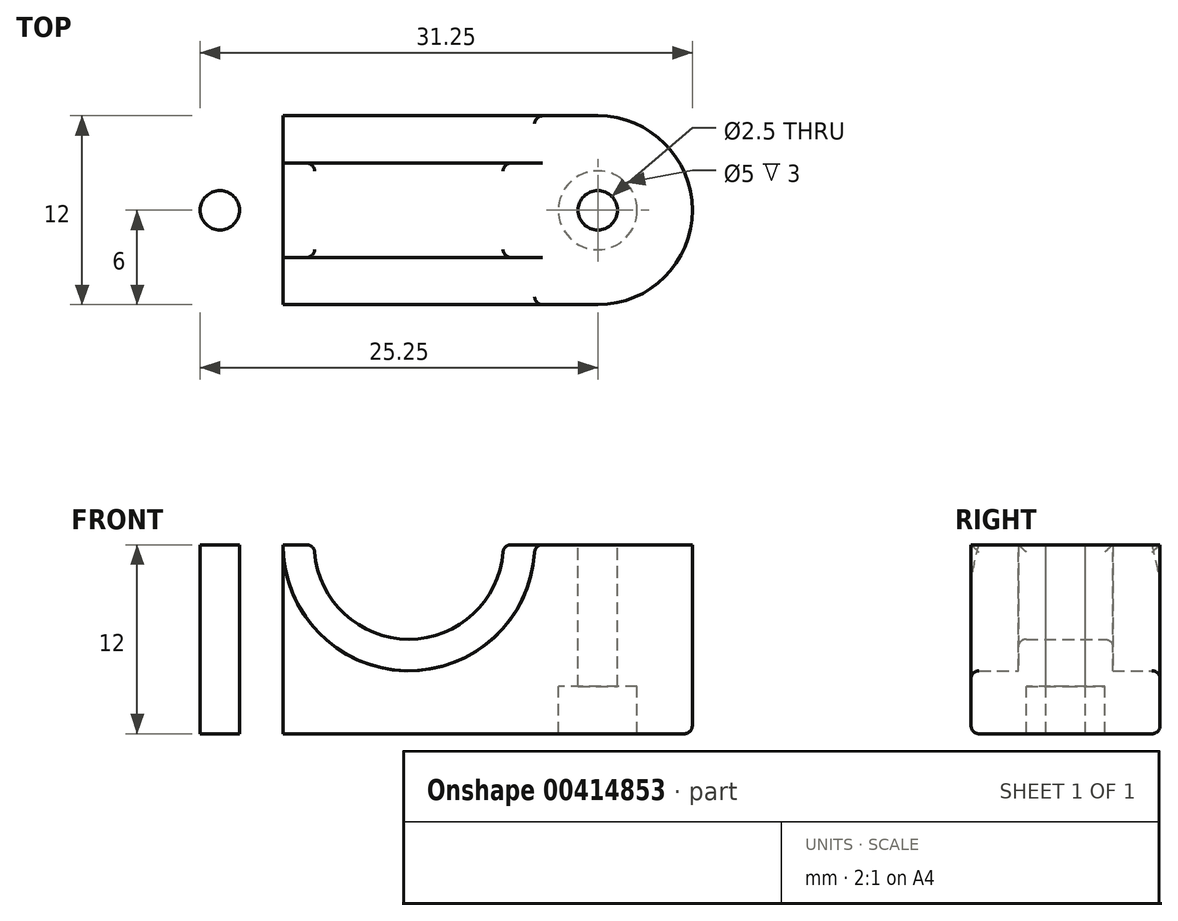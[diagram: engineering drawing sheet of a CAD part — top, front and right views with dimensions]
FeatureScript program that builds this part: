
annotation { "Feature Type Name" : "Feature", "Feature Type Description" : "" }
export const myFeature = defineFeature(function(context is Context, id is Id, definition is map)
    precondition{}
    {
        {
            var Q0;
            Q0=qCreatedBy(makeId("Top.planeOp"),FACE);
            cPlane(context, id + "F0", {"entities" : qUnion([Q0]), "cplaneType" : CPlaneType.OFFSET, "offset" : 1.5 * mm, "oppositeDirection" : true, "width" : 150 * mm, "height" : 150 * mm});
        }
        {
            var Q0;
            Q0=qCreatedBy(makeId("Front.planeOp"),FACE);
            cPlane(context, id + "F1", {"entities" : qUnion([Q0]), "cplaneType" : CPlaneType.OFFSET, "offset" : 12 * mm, "width" : 150 * mm, "height" : 150 * mm});
        }
        {
            var Q0;
            Q0=qCreatedBy(id+"F0.planeOp",FACE);
            var sketch = newSketch(context, id + "F2", { "sketchPlane" : qUnion([Q0])});
            skLineSegment(sketch, "E0.bottom", {"start": v(18, 18) * mm, "end": v(-18, 18) * mm, "construction": true});
            skLineSegment(sketch, "E0.left", {"start": v(18, 18) * mm, "end": v(18, -18) * mm, "construction": true});
            skLineSegment(sketch, "E0.right", {"start": v(-18, 18) * mm, "end": v(-18, -18) * mm, "construction": true});
            skPoint(sketch, "E0.middle", {"position": v(0, 0) * mm});
            skLineSegment(sketch, "E1", {"start": v(-18, 0) * mm, "end": v(18, 0) * mm, "construction": true});
            skLineSegment(sketch, "E2", {"start": v(0, 18) * mm, "end": v(0, -18) * mm, "construction": true});
            skCircle(sketch, "E3", {"center": v(12, -12) * mm, "radius": 1.25 * mm});
            skCircle(sketch, "E4.MirrorC", {"center": v(-12, -12) * mm, "radius": 1.25 * mm});
            skCircle(sketch, "E5", {"center": v(12, 0) * mm, "radius": 1.25 * mm});
            skCircle(sketch, "E6.MirrorC", {"center": v(-12, 0) * mm, "radius": 1.25 * mm});
            skLineSegment(sketch, "E7", {"start": v(-12, 0) * mm, "end": v(12, -12) * mm, "construction": true});
            skLineSegment(sketch, "E8", {"start": v(12, 0) * mm, "end": v(-12, -12) * mm, "construction": true});
            skLineSegment(sketch, "E9", {"start": v(-12, 0) * mm, "end": v(12, 0) * mm, "construction": true});
            skLineSegment(sketch, "E10", {"start": v(0, -6) * mm, "end": v(0, 0) * mm, "construction": true});
            skCircle(sketch, "E11", {"center": v(-12, 0) * mm, "radius": 1.7 * mm, "construction": true});
            skCircle(sketch, "E12", {"center": v(-12, -12) * mm, "radius": 1.7 * mm, "construction": true});
            skCircle(sketch, "E13", {"center": v(12, -12) * mm, "radius": 1.7 * mm, "construction": true});
            skCircle(sketch, "E14", {"center": v(12, 0) * mm, "radius": 1.7 * mm, "construction": true});
            skCircle(sketch, "E15", {"center": v(-12, -12) * mm, "radius": 6 * mm, "construction": true});
            skCircle(sketch, "E16", {"center": v(12, -12) * mm, "radius": 6 * mm, "construction": true});
            skLineSegment(sketch, "E17", {"start": v(-12, -12) * mm, "end": v(12, -12) * mm, "construction": true});
            skLineSegment(sketch, "E18.bottom", {"start": v(12, -18) * mm, "end": v(-12, -18) * mm, "construction": true});
            skLineSegment(sketch, "E18.left", {"start": v(12, -18) * mm, "end": v(12, -6) * mm, "construction": true});
            skLineSegment(sketch, "E18.right", {"start": v(-12, -18) * mm, "end": v(-12, -6) * mm, "construction": true});
            skPoint(sketch, "E18.middle", {"position": v(0, -12) * mm});
            skLineSegment(sketch, "E19", {"start": v(-12, -6) * mm, "end": v(12, -6) * mm});
            skLineSegment(sketch, "E20", {"start": v(12, -18) * mm, "end": v(-12, -18) * mm});
            skArc(sketch, "E21", {"start": v(-12, -6) * mm, "mid": v(-18, -12) * mm, "end": v(-12, -18) * mm});
            skArc(sketch, "E22", {"start": v(12, -6) * mm, "mid": v(18, -12) * mm, "end": v(12, -18) * mm});
            skLineSegment(sketch, "E23.0", {"start": v(-8, 18) * mm, "end": v(-8, -18) * mm, "construction": true});
            skLineSegment(sketch, "E24.0", {"start": v(8, 18) * mm, "end": v(8, -18) * mm, "construction": true});
            skLineSegment(sketch, "E25.0", {"start": v(-12, -15) * mm, "end": v(12, -15) * mm, "construction": true});
            skLineSegment(sketch, "E26.0", {"start": v(-12, -9) * mm, "end": v(12, -9) * mm, "construction": true});
            skLineSegment(sketch, "E27", {"start": v(-8, -6) * mm, "end": v(-8, -9) * mm});
            skLineSegment(sketch, "E28", {"start": v(-8, -9) * mm, "end": v(8, -9) * mm});
            skLineSegment(sketch, "E29", {"start": v(8, -9) * mm, "end": v(8, -6) * mm});
            skLineSegment(sketch, "E30", {"start": v(-8, -18) * mm, "end": v(-8, -15) * mm});
            skLineSegment(sketch, "E31", {"start": v(-8, -15) * mm, "end": v(8, -15) * mm});
            skLineSegment(sketch, "E32", {"start": v(8, -15) * mm, "end": v(8, -18) * mm});
            skLineSegment(sketch, "E33", {"start": v(8, -9) * mm, "end": v(8, -15) * mm});
            skLineSegment(sketch, "E34", {"start": v(-8, -9) * mm, "end": v(-8, -15) * mm});
            skCircle(sketch, "E35.MirrorC", {"center": v(-12, 12) * mm, "radius": 6 * mm, "construction": true});
            skCircle(sketch, "E36.MirrorC", {"center": v(12, 12) * mm, "radius": 6 * mm, "construction": true});
            skArc(sketch, "E37", {"start": v(-18, 12) * mm, "mid": v(-16.24, 16.24) * mm, "end": v(-12, 18) * mm});
            skArc(sketch, "E38", {"start": v(12, 18) * mm, "mid": v(16.24, 16.24) * mm, "end": v(18, 12) * mm});
            skLineSegment(sketch, "E39", {"start": v(-18, -12) * mm, "end": v(-18, 12) * mm});
            skLineSegment(sketch, "E40", {"start": v(-12, 18) * mm, "end": v(12, 18) * mm});
            skLineSegment(sketch, "E41", {"start": v(18, 12) * mm, "end": v(18, -12) * mm});
            skCircle(sketch, "E42", {"center": v(12, 12) * mm, "radius": 1.25 * mm});
            skCircle(sketch, "E43.MirrorC", {"center": v(-12, 12) * mm, "radius": 1.25 * mm});
            skLineSegment(sketch, "E44", {"start": v(-12, 12) * mm, "end": v(12, 0) * mm, "construction": true});
            skLineSegment(sketch, "E45", {"start": v(12, 12) * mm, "end": v(-12, 0) * mm, "construction": true});
            skLineSegment(sketch, "E46", {"start": v(-12, 12) * mm, "end": v(12, 12) * mm, "construction": true});
            skCircle(sketch, "E47", {"center": v(-12, 12) * mm, "radius": 1.7 * mm, "construction": true});
            skCircle(sketch, "E48", {"center": v(12, 12) * mm, "radius": 1.7 * mm, "construction": true});
            skLineSegment(sketch, "E49", {"start": v(-8, 18) * mm, "end": v(-8, -6) * mm});
            skLineSegment(sketch, "E50", {"start": v(8, 18) * mm, "end": v(8, -6) * mm});
            skLineSegment(sketch, "E51", {"start": v(12, -6) * mm, "end": v(18, -6) * mm});
            skLineSegment(sketch, "E52", {"start": v(-12, -6) * mm, "end": v(-18, -6) * mm});
            skLineSegment(sketch, "E53", {"start": v(-8, -18) * mm, "end": v(-8, -37) * mm, "construction": true});
            skLineSegment(sketch, "E54", {"start": v(8, -18) * mm, "end": v(8, -37) * mm, "construction": true});
            skLineSegment(sketch, "E55", {"start": v(-8, -37) * mm, "end": v(8, -37) * mm, "construction": true});
            skCircle(sketch, "E56", {"center": v(0, -20.73) * mm, "radius": 1.25 * mm, "construction": true});
            skCircle(sketch, "E57", {"center": v(12, -12) * mm, "radius": 1.25 * mm, "construction": true});
            skCircle(sketch, "E58.MirrorC", {"center": v(-12, -12) * mm, "radius": 1.25 * mm, "construction": true});
            skCircle(sketch, "E59", {"center": v(0, -4.37) * mm, "radius": 1.25 * mm, "construction": true});
            skCircle(sketch, "E60", {"center": v(0, -12) * mm, "radius": 1.25 * mm, "construction": true});
            skCircle(sketch, "E61", {"center": v(0, 10.9) * mm, "radius": 1.25 * mm, "construction": true});
            skCircle(sketch, "E62", {"center": v(0, 3.27) * mm, "radius": 1.25 * mm, "construction": true});
            skLineSegment(sketch, "E63.bottom", {"start": v(18, 25) * mm, "end": v(-18, 25) * mm, "construction": true});
            skLineSegment(sketch, "E63.top", {"start": v(18, -18) * mm, "end": v(-18, -18) * mm, "construction": true});
            skLineSegment(sketch, "E64", {"start": v(8, 0) * mm, "end": v(-8, 0) * mm});
            skSolve(sketch);
        }
        {
            var Q0;
            Q0=qCreatedBy(id+"F1.planeOp",FACE);
            var sketch = newSketch(context, id + "F3", { "sketchPlane" : qUnion([Q0])});
            skLineSegment(sketch, "E65.bottom", {"start": v(18, -7.5) * mm, "end": v(-18, -7.5) * mm});
            skLineSegment(sketch, "E65.top", {"start": v(18, 7.5) * mm, "end": v(-18, 7.5) * mm, "construction": true});
            skLineSegment(sketch, "E65.left", {"start": v(18, -7.5) * mm, "end": v(18, 7.5) * mm, "construction": true});
            skLineSegment(sketch, "E65.right", {"start": v(-18, -7.5) * mm, "end": v(-18, 7.5) * mm, "construction": true});
            skPoint(sketch, "E65.middle", {"position": v(0, 0) * mm});
            skLineSegment(sketch, "E66", {"start": v(0, 7.5) * mm, "end": v(0, -7.5) * mm, "construction": true});
            skLineSegment(sketch, "E67", {"start": v(-18, 0) * mm, "end": v(18, 0) * mm, "construction": true});
            skCircle(sketch, "E68", {"center": v(0, 7.5) * mm, "radius": 8 * mm, "construction": true});
            skCircle(sketch, "E69", {"center": v(0, 7.5) * mm, "radius": 6 * mm, "construction": true});
            skLineSegment(sketch, "E70.0", {"start": v(-17, -7.5) * mm, "end": v(-17, 7.5) * mm, "construction": true});
            skLineSegment(sketch, "E71.0", {"start": v(-16, -7.5) * mm, "end": v(-16, 7.5) * mm, "construction": true});
            skLineSegment(sketch, "E72.0", {"start": v(18, 6.5) * mm, "end": v(-18, 6.5) * mm, "construction": true});
            skLineSegment(sketch, "E73.0", {"start": v(18, 5.5) * mm, "end": v(-18, 5.5) * mm, "construction": true});
            skLineSegment(sketch, "E74.MirrorCS", {"start": v(16, -7.5) * mm, "end": v(16, 7.5) * mm, "construction": true});
            skLineSegment(sketch, "E75.MirrorCS", {"start": v(17, -7.5) * mm, "end": v(17, 7.5) * mm, "construction": true});
            skArc(sketch, "E76", {"start": v(-17, 7.5) * mm, "mid": v(-17.7, 7.2) * mm, "end": v(-18, 6.5) * mm});
            skArc(sketch, "E77", {"start": v(17, 7.5) * mm, "mid": v(17.7, 7.2) * mm, "end": v(18, 6.5) * mm});
            skLineSegment(sketch, "E78", {"start": v(-18, -7.5) * mm, "end": v(-18, 6.5) * mm});
            skLineSegment(sketch, "E79", {"start": v(-17, 7.5) * mm, "end": v(-6, 7.5) * mm});
            skLineSegment(sketch, "E80", {"start": v(6, 7.5) * mm, "end": v(17, 7.5) * mm});
            skLineSegment(sketch, "E81", {"start": v(18, 6.5) * mm, "end": v(18, -7.5) * mm});
            skArc(sketch, "E82", {"start": v(-8, 7.5) * mm, "mid": v(0, -0.5) * mm, "end": v(8, 7.5) * mm});
            skArc(sketch, "E83", {"start": v(6, 7.5) * mm, "mid": v(0, 1.5) * mm, "end": v(-6, 7.5) * mm});
            skLineSegment(sketch, "E84", {"start": v(-8, 7.5) * mm, "end": v(-8, -1.49) * mm});
            skLineSegment(sketch, "E85", {"start": v(8, -1.49) * mm, "end": v(8, 7.5) * mm});
            skLineSegment(sketch, "E86", {"start": v(-8, -1.49) * mm, "end": v(-8, -7.5) * mm});
            skLineSegment(sketch, "E87", {"start": v(8, -1.49) * mm, "end": v(8, -7.5) * mm});
            skLineSegment(sketch, "E88.MirrorCS", {"start": v(10.5, -1.49) * mm, "end": v(10.5, -7.5) * mm, "construction": true});
            skLineSegment(sketch, "E89", {"start": v(-10.5, -7.5) * mm, "end": v(-10.5, 0) * mm});
            skLineSegment(sketch, "E90.MirrorCS", {"start": v(10.5, -7.5) * mm, "end": v(10.5, 0) * mm});
            skLineSegment(sketch, "E91", {"start": v(-10.5, 0) * mm, "end": v(-2.78, 0) * mm});
            skLineSegment(sketch, "E92", {"start": v(10.5, 0) * mm, "end": v(2.78, 0) * mm});
            skLineSegment(sketch, "E93.0", {"start": v(-8, -1.69) * mm, "end": v(8, -1.69) * mm});
            skSolve(sketch);
        }
        {
            var Q0;
            Q0=makeQuery(id+"F2.imprint","IMPRINT",FACE,{"disambiguationData":[TD([[makeQuery(id+"F2.imprint","IMPRINT",EDGE,{"derivedFrom":sQuery(id+"F2.wireOp",EDGE,"E11")}),-1.0]])]});
            var Q1;
            Q1=makeQuery(id+"F2.imprint","IMPRINT",FACE,{"disambiguationData":[TD([[makeQuery(id+"F2.imprint","IMPRINT",EDGE,{"derivedFrom":sQuery(id+"F2.wireOp",EDGE,"E12")}),-1.0]])]});
            var Q2;
            Q2=makeQuery(id+"F2.imprint","IMPRINT",FACE,{"disambiguationData":[TD([[makeQuery(id+"F2.imprint","IMPRINT",EDGE,{"derivedFrom":sQuery(id+"F2.wireOp",EDGE,"E13")}),-1.0]])]});
            var Q3;
            Q3=makeQuery(id+"F2.imprint","IMPRINT",FACE,{"disambiguationData":[TD([[makeQuery(id+"F2.imprint","IMPRINT",EDGE,{"derivedFrom":sQuery(id+"F2.wireOp",EDGE,"E4.MirrorC")}),1.0]])]});
            var Q4;
            Q4=makeQuery(id+"F2.imprint","IMPRINT",FACE,{"disambiguationData":[TD([[makeQuery(id+"F2.imprint","IMPRINT",EDGE,{"derivedFrom":sQuery(id+"F2.wireOp",EDGE,"E3")}),-1.0]])]});
            var Q5;
            {var subQ0=sQuery(id+"F2.wireOp",EDGE,"E30");Q5=makeQuery(id+"F2.imprint","IMPRINT",FACE,{"disambiguationData":[TD([[makeQuery(id+"F2.imprint","IMPRINT",EDGE,{"derivedFrom":subQ0}),-1.0]])]});}
            var Q6;
            Q6=makeQuery(id+"F2.imprint","IMPRINT",FACE,{"disambiguationData":[TD([[makeQuery(id+"F2.imprint","IMPRINT",EDGE,{"derivedFrom":sQuery(id+"F2.wireOp",EDGE,"E28")}),-1.0]])]});
            var Q7;
            {var subQ0=sQuery(id+"F2.wireOp",EDGE,"E27");Q7=makeQuery(id+"F2.imprint","IMPRINT",FACE,{"disambiguationData":[TD([[makeQuery(id+"F2.imprint","IMPRINT",EDGE,{"derivedFrom":subQ0}),1.0]])]});}
            extrude(context, id + "F4", {"entities" : qUnion([Q0, Q1, Q2, Q3, Q4, Q5, Q6, Q7]), "oppositeDirection" : true, "depth" : 3 * mm});
        }
        {
            var Q0;
            Q0=makeQuery(id+"F2.imprint","IMPRINT",FACE,{"disambiguationData":[TD([[makeQuery(id+"F2.imprint","IMPRINT",EDGE,{"derivedFrom":sQuery(id+"F2.wireOp",EDGE,"E4.MirrorC")}),1.0]])]});
            var Q1;
            Q1=makeQuery(id+"F2.imprint","IMPRINT",FACE,{"disambiguationData":[TD([[makeQuery(id+"F2.imprint","IMPRINT",EDGE,{"derivedFrom":sQuery(id+"F2.wireOp",EDGE,"E3")}),-1.0]])]});
            extrude(context, id + "F5", {"entities" : qUnion([Q0, Q1]), "operationType" : NewBodyOperationType.ADD, "depth" : 9 * mm});
        }
        {
            var Q0;
            Q0=makeQuery(id+"F3.imprint","IMPRINT",FACE,{"disambiguationData":[TD([[makeQuery(id+"F3.imprint","IMPRINT",EDGE,{"derivedFrom":sQuery(id+"F3.wireOp",EDGE,"E82")}),-1.0]])]});
            var Q1;
            {var subQ1=sQuery(id+"F3.wireOp",EDGE,"75Nu91Y9-py98-9ShY-gUlK-ckxOV0G7Wo7s");Q1=makeQuery(id+"F3.imprint","IMPRINT",FACE,{"disambiguationData":[TD([[makeQuery(id+"F3.imprint","IMPRINT",EDGE,{"derivedFrom":subQ1}),1.0]])]});}
            var Q2;
            {var subQ3=sQuery(id+"F3.wireOp",EDGE,"E93.0");Q2=makeQuery(id+"F3.imprint","IMPRINT",FACE,{"disambiguationData":[TD([[makeQuery(id+"F3.imprint","IMPRINT",EDGE,{"derivedFrom":subQ3}),1.0]])]});}
            extrude(context, id + "F6", {"entities" : qUnion([Q0, Q1, Q2]), "operationType" : NewBodyOperationType.ADD, "endBound" : BoundingType.SYMMETRIC, "depth" : 12 * mm});
        }
        {
            var Q0;
            {var subQ2=sQuery(id+"F3.wireOp",EDGE,"E82");Q0=makeQuery(id+"F3.imprint","IMPRINT",FACE,{"disambiguationData":[TD([[makeQuery(id+"F3.imprint","IMPRINT",EDGE,{"derivedFrom":subQ2}),1.0]])]});}
            extrude(context, id + "F7", {"entities" : qUnion([Q0]), "operationType" : NewBodyOperationType.ADD, "endBound" : BoundingType.SYMMETRIC, "depth" : 6 * mm});
        }
        {
            var Q0;
            Q0=makeQuery(id+"FwBo9yE4fHLEFep_69.opExtrude","SWEPT_EDGE",EDGE,{"disambiguationData":[OSD([sQuery(id+"FDGlM9RexINgIxM_69.wireOp",EDGE,"U6KJ8oOa-uFEJ-GBMX-Fjwa-RUX1qTOi3xQP"),sQuery(id+"FDGlM9RexINgIxM_69.wireOp",EDGE,"cxezqcFe-z0Zx-MpOM-KnBF-xNsoa0WWztHi")])]});
            var Q1;
            Q1=makeQuery(id+"FwBo9yE4fHLEFep_69.opExtrude","SWEPT_EDGE",EDGE,{"disambiguationData":[OSD([sQuery(id+"FDGlM9RexINgIxM_69.wireOp",EDGE,"074224ba-19b3-484a-b76f-18158d3281010.MirrorCS"),sQuery(id+"FDGlM9RexINgIxM_69.wireOp",EDGE,"1f1a98b2-39e8-4062-9297-e102a288640b0.MirrorCS")])]});
            var Q2;
            {var subQ0=sQuery(id+"F2.wireOp",EDGE,"E22");var subQ1=sQuery(id+"F2.wireOp",EDGE,"E19");var subQ2=makeQuery(id+"F5.opExtrude","SWEPT_FACE",FACE,{"disambiguationData":[OSD([subQ1]),TDD([makeQuery(id+"F2.imprint","IMPRINT",EDGE,{"disambiguationData":[TD([[makeQuery(id+"F2.imprint","INTERSECT",VERTEX,{"derivedFrom":[subQ1,subQ0,sQuery(id+"F2.wireOp",EDGE,"E51")]}),1.0]])],"derivedFrom":subQ1})])]});var subQ3=makeQuery(id+"F4.opExtrude","SWEPT_FACE",FACE,{"disambiguationData":[OSD([subQ1])]});var subQ4=sQuery(id+"F2.wireOp",EDGE,"E21");var subQ5=makeQuery(id+"F5.opExtrude","SWEPT_FACE",FACE,{"disambiguationData":[OSD([subQ1]),TDD([makeQuery(id+"F2.imprint","IMPRINT",EDGE,{"disambiguationData":[TD([[makeQuery(id+"F2.imprint","INTERSECT",VERTEX,{"derivedFrom":[subQ1,subQ4,sQuery(id+"F2.wireOp",EDGE,"E52")]}),-1.0]])],"derivedFrom":subQ1})])]});var subQ6=makeQuery(id+"F4.opExtrude","CAP_FACE",FACE,{"disambiguationData":[OSD([sQuery(id+"F2.wireOp",EDGE,"E3"),sQuery(id+"F2.wireOp",EDGE,"E4.MirrorC"),subQ1,sQuery(id+"F2.wireOp",EDGE,"E20"),subQ4,subQ0])],"isStart":false});var subQ7=makeQuery(id+"F6.opExtrude","CAP_FACE",FACE,{"disambiguationData":[OSD([sQuery(id+"F3.wireOp",EDGE,"E82"),sQuery(id+"F3.wireOp",EDGE,"E84"),sQuery(id+"F3.wireOp",EDGE,"E85"),sQuery(id+"F3.wireOp",EDGE,"E86"),sQuery(id+"F3.wireOp",EDGE,"E87"),sQuery(id+"F3.wireOp",EDGE,"E93.0")])],"isStart":true});var subQ8=makeQuery(id+"FwBo9yE4fHLEFep_69.opExtrude","SWEPT_FACE",FACE,{"disambiguationData":[OSD([sQuery(id+"FDGlM9RexINgIxM_69.wireOp",EDGE,"074224ba-19b3-484a-b76f-18158d3281010.MirrorCS")])]});Q2=makeQuery(id+"FwBo9yE4fHLEFep_69.boolean.opBoolean","SPLIT",EDGE,{"disambiguationData":[topologyDisambiguationEdgeConnected([subQ6,subQ3,subQ5,subQ2,subQ7,subQ8]),TD([makeQuery(id+"FwBo9yE4fHLEFep_69.opExtrude","SWEPT_FACE",FACE,{"disambiguationData":[OSD([sQuery(id+"FDGlM9RexINgIxM_69.wireOp",EDGE,"qdiU9VLt-Uh7Y-RWx7-BbOI-U16zUYbDfWws")])]})])],"derivedFrom":makeQuery(id+"F4.opExtrude","CAP_EDGE",EDGE,{"disambiguationData":[OSD([subQ1])],"isStart":false})});}
            var Q3;
            {var subQ0=sQuery(id+"F2.wireOp",EDGE,"E21");var subQ1=sQuery(id+"F2.wireOp",EDGE,"E19");var subQ2=makeQuery(id+"F4.opExtrude","SWEPT_FACE",FACE,{"disambiguationData":[OSD([subQ1])]});var subQ3=makeQuery(id+"F5.opExtrude","SWEPT_FACE",FACE,{"disambiguationData":[OSD([subQ1]),TDD([makeQuery(id+"F2.imprint","IMPRINT",EDGE,{"disambiguationData":[TD([[makeQuery(id+"F2.imprint","INTERSECT",VERTEX,{"derivedFrom":[subQ1,subQ0,sQuery(id+"F2.wireOp",EDGE,"E52")]}),-1.0]])],"derivedFrom":subQ1})])]});var subQ4=sQuery(id+"F2.wireOp",EDGE,"E22");var subQ5=makeQuery(id+"F4.opExtrude","CAP_FACE",FACE,{"disambiguationData":[OSD([sQuery(id+"F2.wireOp",EDGE,"E3"),sQuery(id+"F2.wireOp",EDGE,"E4.MirrorC"),subQ1,sQuery(id+"F2.wireOp",EDGE,"E20"),subQ0,subQ4])],"isStart":false});var subQ6=makeQuery(id+"F6.opExtrude","CAP_FACE",FACE,{"disambiguationData":[OSD([sQuery(id+"F3.wireOp",EDGE,"E82"),sQuery(id+"F3.wireOp",EDGE,"E84"),sQuery(id+"F3.wireOp",EDGE,"E85"),sQuery(id+"F3.wireOp",EDGE,"E86"),sQuery(id+"F3.wireOp",EDGE,"E87"),sQuery(id+"F3.wireOp",EDGE,"E93.0")])],"isStart":true});var subQ7=makeQuery(id+"F5.opExtrude","SWEPT_FACE",FACE,{"disambiguationData":[OSD([subQ1]),TDD([makeQuery(id+"F2.imprint","IMPRINT",EDGE,{"disambiguationData":[TD([[makeQuery(id+"F2.imprint","INTERSECT",VERTEX,{"derivedFrom":[subQ1,subQ4,sQuery(id+"F2.wireOp",EDGE,"E51")]}),1.0]])],"derivedFrom":subQ1})])]});var subQ8=makeQuery(id+"FwBo9yE4fHLEFep_69.opExtrude","SWEPT_FACE",FACE,{"disambiguationData":[OSD([sQuery(id+"FDGlM9RexINgIxM_69.wireOp",EDGE,"074224ba-19b3-484a-b76f-18158d3281010.MirrorCS")])]});Q3=makeQuery(id+"FwBo9yE4fHLEFep_69.boolean.opBoolean","SPLIT",EDGE,{"disambiguationData":[topologyDisambiguationEdgeConnected([subQ5,subQ2,subQ3,subQ7,subQ6,subQ8]),TD([makeQuery(id+"F4.opExtrude","SWEPT_FACE",FACE,{"disambiguationData":[OSD([subQ0])]})])],"derivedFrom":makeQuery(id+"F4.opExtrude","CAP_EDGE",EDGE,{"disambiguationData":[OSD([subQ1])],"isStart":false})});}
            var Q4;
            Q4=makeQuery(id+"F4.opExtrude","CAP_EDGE",EDGE,{"disambiguationData":[OSD([sQuery(id+"F2.wireOp",EDGE,"E21")])],"isStart":false});
            var Q5;
            {var subQ0=sQuery(id+"F2.wireOp",EDGE,"E19");var subQ1=makeQuery(id+"F4.opExtrude","SWEPT_FACE",FACE,{"disambiguationData":[OSD([subQ0])]});var subQ2=sQuery(id+"F2.wireOp",EDGE,"E22");var subQ3=sQuery(id+"F2.wireOp",EDGE,"E21");var subQ4=makeQuery(id+"F5.opExtrude","SWEPT_FACE",FACE,{"disambiguationData":[OSD([subQ0]),TDD([makeQuery(id+"F2.imprint","IMPRINT",EDGE,{"disambiguationData":[TD([[makeQuery(id+"F2.imprint","INTERSECT",VERTEX,{"derivedFrom":[subQ0,subQ3,sQuery(id+"F2.wireOp",EDGE,"E52")]}),-1.0]])],"derivedFrom":subQ0})])]});var subQ5=makeQuery(id+"F4.opExtrude","CAP_FACE",FACE,{"disambiguationData":[OSD([sQuery(id+"F2.wireOp",EDGE,"E3"),sQuery(id+"F2.wireOp",EDGE,"E4.MirrorC"),subQ0,sQuery(id+"F2.wireOp",EDGE,"E20"),subQ3,subQ2])],"isStart":false});var subQ6=makeQuery(id+"F6.opExtrude","CAP_FACE",FACE,{"disambiguationData":[OSD([sQuery(id+"F3.wireOp",EDGE,"E82"),sQuery(id+"F3.wireOp",EDGE,"E84"),sQuery(id+"F3.wireOp",EDGE,"E85"),sQuery(id+"F3.wireOp",EDGE,"E86"),sQuery(id+"F3.wireOp",EDGE,"E87"),sQuery(id+"F3.wireOp",EDGE,"E93.0")])],"isStart":true});var subQ7=makeQuery(id+"F5.opExtrude","SWEPT_FACE",FACE,{"disambiguationData":[OSD([subQ0]),TDD([makeQuery(id+"F2.imprint","IMPRINT",EDGE,{"disambiguationData":[TD([[makeQuery(id+"F2.imprint","INTERSECT",VERTEX,{"derivedFrom":[subQ0,subQ2,sQuery(id+"F2.wireOp",EDGE,"E51")]}),1.0]])],"derivedFrom":subQ0})])]});var subQ8=makeQuery(id+"FwBo9yE4fHLEFep_69.opExtrude","SWEPT_FACE",FACE,{"disambiguationData":[OSD([sQuery(id+"FDGlM9RexINgIxM_69.wireOp",EDGE,"074224ba-19b3-484a-b76f-18158d3281010.MirrorCS")])]});Q5=makeQuery(id+"FwBo9yE4fHLEFep_69.boolean.opBoolean","SPLIT",EDGE,{"disambiguationData":[topologyDisambiguationEdgeConnected([subQ5,subQ1,subQ4,subQ7,subQ6,subQ8]),TD([makeQuery(id+"F4.opExtrude","SWEPT_FACE",FACE,{"disambiguationData":[OSD([subQ2])]})])],"derivedFrom":makeQuery(id+"F4.opExtrude","CAP_EDGE",EDGE,{"disambiguationData":[OSD([subQ0])],"isStart":false})});}
            var Q6;
            Q6=makeQuery(id+"F4.opExtrude","CAP_EDGE",EDGE,{"disambiguationData":[OSD([sQuery(id+"F2.wireOp",EDGE,"E22")])],"isStart":false});
            var Q7;
            Q7=makeQuery(id+"F4.opExtrude","CAP_EDGE",EDGE,{"disambiguationData":[OSD([sQuery(id+"F2.wireOp",EDGE,"E20")])],"isStart":false});
            var Q8;
            Q8=makeQuery(id+"FvI2ILcVgUqUSgN_69.opExtrude","CAP_EDGE",EDGE,{"disambiguationData":[OSD([sQuery(id+"FDGlM9RexINgIxM_69.wireOp",EDGE,"TuuTUsh2-wWyv-E5XA-lqRk-08UfCgmNTLkA")])],"isStart":true});
            var Q9;
            Q9=makeQuery(id+"FwBo9yE4fHLEFep_69.opExtrude","CAP_EDGE",EDGE,{"disambiguationData":[OSD([sQuery(id+"FDGlM9RexINgIxM_69.wireOp",EDGE,"cxezqcFe-z0Zx-MpOM-KnBF-xNsoa0WWztHi")])],"isStart":true});
            var Q10;
            {var subQ0=sQuery(id+"FDGlM9RexINgIxM_69.wireOp",EDGE,"SDjRlF2p-qF32-9Ua2-Iwv7-xdcJq4eqXBu1");var subQ1=sQuery(id+"FDGlM9RexINgIxM_69.wireOp",EDGE,"542167bc-9219-4481-ab75-8efcb1e341040.MirrorCS");var subQ2=sQuery(id+"FDGlM9RexINgIxM_69.wireOp",EDGE,"qdiU9VLt-Uh7Y-RWx7-BbOI-U16zUYbDfWws");var subQ3=sQuery(id+"FDGlM9RexINgIxM_69.wireOp",EDGE,"3RWh9Hf1-zJBz-Ywhi-QnFQ-NlyL1Vy412u8");var subQ4=sQuery(id+"FDGlM9RexINgIxM_69.wireOp",EDGE,"FMMBFegk-woH6-BbVv-6LVj-WN5v0U1wJKbZ");Q10=makeQuery(id+"FwvY9zCnafUxNxe_69.opFillet","BLEND_EDGE",EDGE,{"blendedFrom":[makeQuery(id+"FwBo9yE4fHLEFep_69.opExtrude","SWEPT_EDGE",EDGE,{"disambiguationData":[OSD([subQ4,subQ3])]}),makeQuery(id+"FvI2ILcVgUqUSgN_69.boolean.opBoolean","MERGE",FACE,{"derivedFrom":[makeQuery(id+"FwBo9yE4fHLEFep_69.opExtrude","CAP_FACE",FACE,{"disambiguationData":[OSD([subQ2,subQ0,sQuery(id+"FDGlM9RexINgIxM_69.wireOp",EDGE,"2Y4vgDR9-0Dmv-XGgg-KAib-3JB6RqfQyO1x"),sQuery(id+"FDGlM9RexINgIxM_69.wireOp",EDGE,"qXeFSDnR-qICX-DEm8-lWfQ-4HK4tKIROyhM"),sQuery(id+"FDGlM9RexINgIxM_69.wireOp",EDGE,"074224ba-19b3-484a-b76f-18158d3281010.MirrorCS"),sQuery(id+"FDGlM9RexINgIxM_69.wireOp",EDGE,"1f1a98b2-39e8-4062-9297-e102a288640b0.MirrorCS")])],"isStart":true}),makeQuery(id+"FwBo9yE4fHLEFep_69.opExtrude","CAP_FACE",FACE,{"disambiguationData":[OSD([subQ1,subQ0,subQ4,subQ3,sQuery(id+"FDGlM9RexINgIxM_69.wireOp",EDGE,"U6KJ8oOa-uFEJ-GBMX-Fjwa-RUX1qTOi3xQP"),sQuery(id+"FDGlM9RexINgIxM_69.wireOp",EDGE,"cxezqcFe-z0Zx-MpOM-KnBF-xNsoa0WWztHi")])],"isStart":true}),makeQuery(id+"FvI2ILcVgUqUSgN_69.opExtrude","CAP_FACE",FACE,{"disambiguationData":[OSD([subQ2,subQ1,sQuery(id+"FDGlM9RexINgIxM_69.wireOp",EDGE,"0StFWCpq-pooK-kmjC-ZOlJ-aV2eWWANgGMq"),sQuery(id+"FDGlM9RexINgIxM_69.wireOp",EDGE,"34e925ed-6902-4293-8552-f707c8cda2770.MirrorCS"),sQuery(id+"FDGlM9RexINgIxM_69.wireOp",EDGE,"WwcenAgb-iahb-npIA-mZoE-YonAKNzFRoHx"),subQ0,sQuery(id+"FDGlM9RexINgIxM_69.wireOp",EDGE,"TuuTUsh2-wWyv-E5XA-lqRk-08UfCgmNTLkA")])],"isStart":true})]})],"blendedInto":[makeQuery(id+"FvI2ILcVgUqUSgN_69.boolean.opBoolean","MERGE",FACE,{"derivedFrom":[makeQuery(id+"FwBo9yE4fHLEFep_69.opExtrude","CAP_FACE",FACE,{"disambiguationData":[OSD([subQ2,subQ0,sQuery(id+"FDGlM9RexINgIxM_69.wireOp",EDGE,"2Y4vgDR9-0Dmv-XGgg-KAib-3JB6RqfQyO1x"),sQuery(id+"FDGlM9RexINgIxM_69.wireOp",EDGE,"qXeFSDnR-qICX-DEm8-lWfQ-4HK4tKIROyhM"),sQuery(id+"FDGlM9RexINgIxM_69.wireOp",EDGE,"074224ba-19b3-484a-b76f-18158d3281010.MirrorCS"),sQuery(id+"FDGlM9RexINgIxM_69.wireOp",EDGE,"1f1a98b2-39e8-4062-9297-e102a288640b0.MirrorCS")])],"isStart":true}),makeQuery(id+"FwBo9yE4fHLEFep_69.opExtrude","CAP_FACE",FACE,{"disambiguationData":[OSD([subQ1,subQ0,subQ4,subQ3,sQuery(id+"FDGlM9RexINgIxM_69.wireOp",EDGE,"U6KJ8oOa-uFEJ-GBMX-Fjwa-RUX1qTOi3xQP"),sQuery(id+"FDGlM9RexINgIxM_69.wireOp",EDGE,"cxezqcFe-z0Zx-MpOM-KnBF-xNsoa0WWztHi")])],"isStart":true}),makeQuery(id+"FvI2ILcVgUqUSgN_69.opExtrude","CAP_FACE",FACE,{"disambiguationData":[OSD([subQ2,subQ1,sQuery(id+"FDGlM9RexINgIxM_69.wireOp",EDGE,"0StFWCpq-pooK-kmjC-ZOlJ-aV2eWWANgGMq"),sQuery(id+"FDGlM9RexINgIxM_69.wireOp",EDGE,"34e925ed-6902-4293-8552-f707c8cda2770.MirrorCS"),sQuery(id+"FDGlM9RexINgIxM_69.wireOp",EDGE,"WwcenAgb-iahb-npIA-mZoE-YonAKNzFRoHx"),subQ0,sQuery(id+"FDGlM9RexINgIxM_69.wireOp",EDGE,"TuuTUsh2-wWyv-E5XA-lqRk-08UfCgmNTLkA")])],"isStart":true})]})]});}
            var Q11;
            Q11=makeQuery(id+"FwBo9yE4fHLEFep_69.opExtrude","CAP_EDGE",EDGE,{"disambiguationData":[OSD([sQuery(id+"FDGlM9RexINgIxM_69.wireOp",EDGE,"1f1a98b2-39e8-4062-9297-e102a288640b0.MirrorCS")])],"isStart":true});
            var Q12;
            {var subQ0=sQuery(id+"FDGlM9RexINgIxM_69.wireOp",EDGE,"SDjRlF2p-qF32-9Ua2-Iwv7-xdcJq4eqXBu1");var subQ1=sQuery(id+"FDGlM9RexINgIxM_69.wireOp",EDGE,"542167bc-9219-4481-ab75-8efcb1e341040.MirrorCS");var subQ2=sQuery(id+"FDGlM9RexINgIxM_69.wireOp",EDGE,"qdiU9VLt-Uh7Y-RWx7-BbOI-U16zUYbDfWws");var subQ3=sQuery(id+"FDGlM9RexINgIxM_69.wireOp",EDGE,"qXeFSDnR-qICX-DEm8-lWfQ-4HK4tKIROyhM");var subQ4=sQuery(id+"FDGlM9RexINgIxM_69.wireOp",EDGE,"2Y4vgDR9-0Dmv-XGgg-KAib-3JB6RqfQyO1x");Q12=makeQuery(id+"FwvY9zCnafUxNxe_69.opFillet","BLEND_EDGE",EDGE,{"blendedFrom":[makeQuery(id+"FwBo9yE4fHLEFep_69.opExtrude","SWEPT_EDGE",EDGE,{"disambiguationData":[OSD([subQ4,subQ3])]}),makeQuery(id+"FvI2ILcVgUqUSgN_69.boolean.opBoolean","MERGE",FACE,{"derivedFrom":[makeQuery(id+"FwBo9yE4fHLEFep_69.opExtrude","CAP_FACE",FACE,{"disambiguationData":[OSD([subQ2,subQ0,subQ4,subQ3,sQuery(id+"FDGlM9RexINgIxM_69.wireOp",EDGE,"074224ba-19b3-484a-b76f-18158d3281010.MirrorCS"),sQuery(id+"FDGlM9RexINgIxM_69.wireOp",EDGE,"1f1a98b2-39e8-4062-9297-e102a288640b0.MirrorCS")])],"isStart":true}),makeQuery(id+"FwBo9yE4fHLEFep_69.opExtrude","CAP_FACE",FACE,{"disambiguationData":[OSD([subQ1,subQ0,sQuery(id+"FDGlM9RexINgIxM_69.wireOp",EDGE,"FMMBFegk-woH6-BbVv-6LVj-WN5v0U1wJKbZ"),sQuery(id+"FDGlM9RexINgIxM_69.wireOp",EDGE,"3RWh9Hf1-zJBz-Ywhi-QnFQ-NlyL1Vy412u8"),sQuery(id+"FDGlM9RexINgIxM_69.wireOp",EDGE,"U6KJ8oOa-uFEJ-GBMX-Fjwa-RUX1qTOi3xQP"),sQuery(id+"FDGlM9RexINgIxM_69.wireOp",EDGE,"cxezqcFe-z0Zx-MpOM-KnBF-xNsoa0WWztHi")])],"isStart":true}),makeQuery(id+"FvI2ILcVgUqUSgN_69.opExtrude","CAP_FACE",FACE,{"disambiguationData":[OSD([subQ2,subQ1,sQuery(id+"FDGlM9RexINgIxM_69.wireOp",EDGE,"0StFWCpq-pooK-kmjC-ZOlJ-aV2eWWANgGMq"),sQuery(id+"FDGlM9RexINgIxM_69.wireOp",EDGE,"34e925ed-6902-4293-8552-f707c8cda2770.MirrorCS"),sQuery(id+"FDGlM9RexINgIxM_69.wireOp",EDGE,"WwcenAgb-iahb-npIA-mZoE-YonAKNzFRoHx"),subQ0,sQuery(id+"FDGlM9RexINgIxM_69.wireOp",EDGE,"TuuTUsh2-wWyv-E5XA-lqRk-08UfCgmNTLkA")])],"isStart":true})]})],"blendedInto":[makeQuery(id+"FvI2ILcVgUqUSgN_69.boolean.opBoolean","MERGE",FACE,{"derivedFrom":[makeQuery(id+"FwBo9yE4fHLEFep_69.opExtrude","CAP_FACE",FACE,{"disambiguationData":[OSD([subQ2,subQ0,subQ4,subQ3,sQuery(id+"FDGlM9RexINgIxM_69.wireOp",EDGE,"074224ba-19b3-484a-b76f-18158d3281010.MirrorCS"),sQuery(id+"FDGlM9RexINgIxM_69.wireOp",EDGE,"1f1a98b2-39e8-4062-9297-e102a288640b0.MirrorCS")])],"isStart":true}),makeQuery(id+"FwBo9yE4fHLEFep_69.opExtrude","CAP_FACE",FACE,{"disambiguationData":[OSD([subQ1,subQ0,sQuery(id+"FDGlM9RexINgIxM_69.wireOp",EDGE,"FMMBFegk-woH6-BbVv-6LVj-WN5v0U1wJKbZ"),sQuery(id+"FDGlM9RexINgIxM_69.wireOp",EDGE,"3RWh9Hf1-zJBz-Ywhi-QnFQ-NlyL1Vy412u8"),sQuery(id+"FDGlM9RexINgIxM_69.wireOp",EDGE,"U6KJ8oOa-uFEJ-GBMX-Fjwa-RUX1qTOi3xQP"),sQuery(id+"FDGlM9RexINgIxM_69.wireOp",EDGE,"cxezqcFe-z0Zx-MpOM-KnBF-xNsoa0WWztHi")])],"isStart":true}),makeQuery(id+"FvI2ILcVgUqUSgN_69.opExtrude","CAP_FACE",FACE,{"disambiguationData":[OSD([subQ2,subQ1,sQuery(id+"FDGlM9RexINgIxM_69.wireOp",EDGE,"0StFWCpq-pooK-kmjC-ZOlJ-aV2eWWANgGMq"),sQuery(id+"FDGlM9RexINgIxM_69.wireOp",EDGE,"34e925ed-6902-4293-8552-f707c8cda2770.MirrorCS"),sQuery(id+"FDGlM9RexINgIxM_69.wireOp",EDGE,"WwcenAgb-iahb-npIA-mZoE-YonAKNzFRoHx"),subQ0,sQuery(id+"FDGlM9RexINgIxM_69.wireOp",EDGE,"TuuTUsh2-wWyv-E5XA-lqRk-08UfCgmNTLkA")])],"isStart":true})]})]});}
            var Q13;
            Q13=makeQuery(id+"FvI2ILcVgUqUSgN_69.opExtrude","CAP_EDGE",EDGE,{"disambiguationData":[OSD([sQuery(id+"FDGlM9RexINgIxM_69.wireOp",EDGE,"WwcenAgb-iahb-npIA-mZoE-YonAKNzFRoHx")])],"isStart":false});
            var Q14;
            Q14=makeQuery(id+"F7.opExtrude","CAP_EDGE",EDGE,{"disambiguationData":[OSD([sQuery(id+"F3.wireOp",EDGE,"E83")])],"isStart":true});
            var Q15;
            Q15=makeQuery(id+"F7.opExtrude","CAP_EDGE",EDGE,{"disambiguationData":[OSD([sQuery(id+"F3.wireOp",EDGE,"E83")])],"isStart":false});
            var Q16;
            Q16=makeQuery(id+"F7.opExtrude","SWEPT_EDGE",EDGE,{"disambiguationData":[OSD([sQuery(id+"F3.wireOp",EDGE,"E80"),sQuery(id+"F3.wireOp",EDGE,"E83")])]});
            var Q17;
            Q17=makeQuery(id+"F7.opExtrude","SWEPT_EDGE",EDGE,{"disambiguationData":[OSD([sQuery(id+"F3.wireOp",EDGE,"E79"),sQuery(id+"F3.wireOp",EDGE,"E83")])]});
            var Q18;
            Q18=makeQuery(id+"F6.opExtrude","CAP_EDGE",EDGE,{"disambiguationData":[OSD([sQuery(id+"F3.wireOp",EDGE,"E82")])],"isStart":false});
            var Q19;
            Q19=makeQuery(id+"F6.opExtrude","CAP_EDGE",EDGE,{"disambiguationData":[OSD([sQuery(id+"F3.wireOp",EDGE,"E82")])],"isStart":true});
            var Q20;
            {var subQ0=sQuery(id+"F2.wireOp",EDGE,"E19");var subQ1=sQuery(id+"F3.wireOp",EDGE,"E82");var subQ2=sQuery(id+"F3.wireOp",EDGE,"E80");var subQ4=sQuery(id+"F2.wireOp",EDGE,"E29");var subQ5=sQuery(id+"F2.wireOp",EDGE,"E33");var subQ6=sQuery(id+"F2.wireOp",EDGE,"E32");var subQ7=sQuery(id+"F3.wireOp",EDGE,"E85");Q20=makeQuery(id+"F7.boolean.opBoolean","SPLIT",EDGE,{"disambiguationData":[TD([makeQuery(id+"F4.opExtrude","SWEPT_FACE",FACE,{"disambiguationData":[OSD([subQ0])]})])],"derivedFrom":makeQuery(id+"F6.boolean.opBoolean","MERGE",EDGE,{"derivedFrom":[makeQuery(id+"F5.opExtrude","CAP_EDGE",EDGE,{"disambiguationData":[OSD([subQ4,subQ6,subQ5])],"isStart":false}),makeQuery(id+"F6.opExtrude","SWEPT_EDGE",EDGE,{"disambiguationData":[OSD([subQ2,subQ1,subQ7])]})]})});}
            var Q21;
            {var subQ1=sQuery(id+"F2.wireOp",EDGE,"E20");var subQ2=sQuery(id+"F2.wireOp",EDGE,"E32");var subQ3=sQuery(id+"F3.wireOp",EDGE,"E82");var subQ4=sQuery(id+"F3.wireOp",EDGE,"E80");var subQ5=sQuery(id+"F2.wireOp",EDGE,"E33");var subQ6=sQuery(id+"F2.wireOp",EDGE,"E29");var subQ7=sQuery(id+"F3.wireOp",EDGE,"E85");Q21=makeQuery(id+"F7.boolean.opBoolean","SPLIT",EDGE,{"disambiguationData":[TD([makeQuery(id+"F4.opExtrude","SWEPT_FACE",FACE,{"disambiguationData":[OSD([subQ1])]})])],"derivedFrom":makeQuery(id+"F6.boolean.opBoolean","MERGE",EDGE,{"derivedFrom":[makeQuery(id+"F5.opExtrude","CAP_EDGE",EDGE,{"disambiguationData":[OSD([subQ6,subQ2,subQ5])],"isStart":false}),makeQuery(id+"F6.opExtrude","SWEPT_EDGE",EDGE,{"disambiguationData":[OSD([subQ4,subQ3,subQ7])]})]})});}
            var Q22;
            {var subQ0=sQuery(id+"F2.wireOp",EDGE,"E20");var subQ1=sQuery(id+"F3.wireOp",EDGE,"E82");var subQ2=sQuery(id+"F2.wireOp",EDGE,"E34");var subQ3=sQuery(id+"F2.wireOp",EDGE,"E30");var subQ4=sQuery(id+"F2.wireOp",EDGE,"E27");var subQ6=sQuery(id+"F3.wireOp",EDGE,"E79");var subQ7=sQuery(id+"F3.wireOp",EDGE,"E84");Q22=makeQuery(id+"F7.boolean.opBoolean","SPLIT",EDGE,{"disambiguationData":[TD([makeQuery(id+"F4.opExtrude","SWEPT_FACE",FACE,{"disambiguationData":[OSD([subQ0])]})])],"derivedFrom":makeQuery(id+"F6.boolean.opBoolean","MERGE",EDGE,{"derivedFrom":[makeQuery(id+"F5.opExtrude","CAP_EDGE",EDGE,{"disambiguationData":[OSD([subQ4,subQ3,subQ2])],"isStart":false}),makeQuery(id+"F6.opExtrude","SWEPT_EDGE",EDGE,{"disambiguationData":[OSD([subQ6,subQ1,subQ7])]})]})});}
            var Q23;
            Q23=makeQuery(id+"FvI2ILcVgUqUSgN_69.opExtrude","CAP_EDGE",EDGE,{"disambiguationData":[OSD([sQuery(id+"FDGlM9RexINgIxM_69.wireOp",EDGE,"TuuTUsh2-wWyv-E5XA-lqRk-08UfCgmNTLkA")])],"isStart":false});
            var Q24;
            Q24=makeQuery(id+"FvI2ILcVgUqUSgN_69.opExtrude","CAP_EDGE",EDGE,{"disambiguationData":[OSD([sQuery(id+"FDGlM9RexINgIxM_69.wireOp",EDGE,"orqZ82ov-6jOO-0uzi-E4WA-3w5yYGLxRUzb")])],"isStart":false});
            var Q25;
            {var subQ0=sQuery(id+"FDGlM9RexINgIxM_69.wireOp",EDGE,"7Ez0brCt-yI1f-XIkG-d1V6-Qcpqxc8gj9kZ");Q25=makeQuery(id+"FvI2ILcVgUqUSgN_69.opExtrude","CAP_EDGE",EDGE,{"disambiguationData":[OSD([subQ0]),TDD([makeQuery(id+"FDGlM9RexINgIxM_69.imprint","IMPRINT",EDGE,{"disambiguationData":[TD([[makeQuery(id+"FDGlM9RexINgIxM_69.imprint","INTERSECT",VERTEX,{"derivedFrom":[subQ0,sQuery(id+"FDGlM9RexINgIxM_69.wireOp",EDGE,"RLFlzvnA-SoUq-z0e6-HeU4-ZmLq0tj3zLtU")]}),-1.0]])],"derivedFrom":subQ0})])],"isStart":false});}
            var Q26;
            {var subQ0=sQuery(id+"FDGlM9RexINgIxM_69.wireOp",EDGE,"RLFlzvnA-SoUq-z0e6-HeU4-ZmLq0tj3zLtU");var subQ1=sQuery(id+"FDGlM9RexINgIxM_69.wireOp",EDGE,"7Ez0brCt-yI1f-XIkG-d1V6-Qcpqxc8gj9kZ");Q26=makeQuery(id+"FwvY9zCnafUxNxe_69.opFillet","BLEND_EDGE",EDGE,{"blendedFrom":[makeQuery(id+"FvI2ILcVgUqUSgN_69.boolean.opBoolean","MERGE",EDGE,{"derivedFrom":[makeQuery(id+"FwBo9yE4fHLEFep_69.opExtrude","SWEPT_EDGE",EDGE,{"disambiguationData":[OSD([subQ1,subQ0])]}),makeQuery(id+"FvI2ILcVgUqUSgN_69.opExtrude","SWEPT_EDGE",EDGE,{"disambiguationData":[OSD([subQ1,subQ0])]})]}),makeQuery(id+"FvI2ILcVgUqUSgN_69.opExtrude","CAP_FACE",FACE,{"disambiguationData":[OSD([sQuery(id+"FDGlM9RexINgIxM_69.wireOp",EDGE,"U6KJ8oOa-uFEJ-GBMX-Fjwa-RUX1qTOi3xQP"),sQuery(id+"FDGlM9RexINgIxM_69.wireOp",EDGE,"074224ba-19b3-484a-b76f-18158d3281010.MirrorCS"),sQuery(id+"FDGlM9RexINgIxM_69.wireOp",EDGE,"TuuTUsh2-wWyv-E5XA-lqRk-08UfCgmNTLkA"),sQuery(id+"FDGlM9RexINgIxM_69.wireOp",EDGE,"FdSPzIjc-Apuu-YrM7-Z5xT-Lyi4e0NFlyLR"),subQ1,subQ0,sQuery(id+"FDGlM9RexINgIxM_69.wireOp",EDGE,"2hJP9DgW-dI3q-Z07M-86yl-LCIOIgQcvf8C"),sQuery(id+"FDGlM9RexINgIxM_69.wireOp",EDGE,"yaoq47ei-afsS-ui4j-o2Ug-eN81qBYXd8bz"),sQuery(id+"FDGlM9RexINgIxM_69.wireOp",EDGE,"qSYrSfl7-yjqs-UGFy-c140-ZDuUcCQf7A2A"),sQuery(id+"FDGlM9RexINgIxM_69.wireOp",EDGE,"itTMaZda-B3PT-bgKm-7mmb-3rBEcSrfuZUN"),sQuery(id+"FDGlM9RexINgIxM_69.wireOp",EDGE,"C7O0F2G3-Vpph-GHgU-Pl9N-YHT5ADbRXPIf"),sQuery(id+"FDGlM9RexINgIxM_69.wireOp",EDGE,"orqZ82ov-6jOO-0uzi-E4WA-3w5yYGLxRUzb"),sQuery(id+"FDGlM9RexINgIxM_69.wireOp",EDGE,"c01c7ff9-4d20-4461-8e9a-ae817acbc2570.MirrorCS")])],"isStart":false})],"blendedInto":[makeQuery(id+"FvI2ILcVgUqUSgN_69.opExtrude","CAP_FACE",FACE,{"disambiguationData":[OSD([sQuery(id+"FDGlM9RexINgIxM_69.wireOp",EDGE,"U6KJ8oOa-uFEJ-GBMX-Fjwa-RUX1qTOi3xQP"),sQuery(id+"FDGlM9RexINgIxM_69.wireOp",EDGE,"074224ba-19b3-484a-b76f-18158d3281010.MirrorCS"),sQuery(id+"FDGlM9RexINgIxM_69.wireOp",EDGE,"TuuTUsh2-wWyv-E5XA-lqRk-08UfCgmNTLkA"),sQuery(id+"FDGlM9RexINgIxM_69.wireOp",EDGE,"FdSPzIjc-Apuu-YrM7-Z5xT-Lyi4e0NFlyLR"),subQ1,subQ0,sQuery(id+"FDGlM9RexINgIxM_69.wireOp",EDGE,"2hJP9DgW-dI3q-Z07M-86yl-LCIOIgQcvf8C"),sQuery(id+"FDGlM9RexINgIxM_69.wireOp",EDGE,"yaoq47ei-afsS-ui4j-o2Ug-eN81qBYXd8bz"),sQuery(id+"FDGlM9RexINgIxM_69.wireOp",EDGE,"qSYrSfl7-yjqs-UGFy-c140-ZDuUcCQf7A2A"),sQuery(id+"FDGlM9RexINgIxM_69.wireOp",EDGE,"itTMaZda-B3PT-bgKm-7mmb-3rBEcSrfuZUN"),sQuery(id+"FDGlM9RexINgIxM_69.wireOp",EDGE,"C7O0F2G3-Vpph-GHgU-Pl9N-YHT5ADbRXPIf"),sQuery(id+"FDGlM9RexINgIxM_69.wireOp",EDGE,"orqZ82ov-6jOO-0uzi-E4WA-3w5yYGLxRUzb"),sQuery(id+"FDGlM9RexINgIxM_69.wireOp",EDGE,"c01c7ff9-4d20-4461-8e9a-ae817acbc2570.MirrorCS")])],"isStart":false})]});}
            var Q27;
            Q27=makeQuery(id+"FvI2ILcVgUqUSgN_69.opExtrude","CAP_EDGE",EDGE,{"disambiguationData":[OSD([sQuery(id+"FDGlM9RexINgIxM_69.wireOp",EDGE,"c01c7ff9-4d20-4461-8e9a-ae817acbc2570.MirrorCS")])],"isStart":false});
            var Q28;
            {var subQ0=sQuery(id+"FDGlM9RexINgIxM_69.wireOp",EDGE,"7Ez0brCt-yI1f-XIkG-d1V6-Qcpqxc8gj9kZ");Q28=makeQuery(id+"FvI2ILcVgUqUSgN_69.opExtrude","CAP_EDGE",EDGE,{"disambiguationData":[OSD([subQ0]),TDD([makeQuery(id+"FDGlM9RexINgIxM_69.imprint","IMPRINT",EDGE,{"disambiguationData":[TD([[makeQuery(id+"FDGlM9RexINgIxM_69.imprint","INTERSECT",VERTEX,{"derivedFrom":[subQ0,sQuery(id+"FDGlM9RexINgIxM_69.wireOp",EDGE,"qSYrSfl7-yjqs-UGFy-c140-ZDuUcCQf7A2A")]}),1.0]])],"derivedFrom":subQ0})])],"isStart":false});}
            var Q29;
            {var subQ0=sQuery(id+"FDGlM9RexINgIxM_69.wireOp",EDGE,"qSYrSfl7-yjqs-UGFy-c140-ZDuUcCQf7A2A");var subQ1=sQuery(id+"FDGlM9RexINgIxM_69.wireOp",EDGE,"7Ez0brCt-yI1f-XIkG-d1V6-Qcpqxc8gj9kZ");Q29=makeQuery(id+"FwvY9zCnafUxNxe_69.opFillet","BLEND_EDGE",EDGE,{"blendedFrom":[makeQuery(id+"FvI2ILcVgUqUSgN_69.boolean.opBoolean","MERGE",EDGE,{"derivedFrom":[makeQuery(id+"FwBo9yE4fHLEFep_69.opExtrude","SWEPT_EDGE",EDGE,{"disambiguationData":[OSD([subQ1,subQ0])]}),makeQuery(id+"FvI2ILcVgUqUSgN_69.opExtrude","SWEPT_EDGE",EDGE,{"disambiguationData":[OSD([subQ1,subQ0])]})]}),makeQuery(id+"FvI2ILcVgUqUSgN_69.opExtrude","CAP_FACE",FACE,{"disambiguationData":[OSD([sQuery(id+"FDGlM9RexINgIxM_69.wireOp",EDGE,"U6KJ8oOa-uFEJ-GBMX-Fjwa-RUX1qTOi3xQP"),sQuery(id+"FDGlM9RexINgIxM_69.wireOp",EDGE,"074224ba-19b3-484a-b76f-18158d3281010.MirrorCS"),sQuery(id+"FDGlM9RexINgIxM_69.wireOp",EDGE,"TuuTUsh2-wWyv-E5XA-lqRk-08UfCgmNTLkA"),sQuery(id+"FDGlM9RexINgIxM_69.wireOp",EDGE,"FdSPzIjc-Apuu-YrM7-Z5xT-Lyi4e0NFlyLR"),subQ1,sQuery(id+"FDGlM9RexINgIxM_69.wireOp",EDGE,"RLFlzvnA-SoUq-z0e6-HeU4-ZmLq0tj3zLtU"),sQuery(id+"FDGlM9RexINgIxM_69.wireOp",EDGE,"2hJP9DgW-dI3q-Z07M-86yl-LCIOIgQcvf8C"),sQuery(id+"FDGlM9RexINgIxM_69.wireOp",EDGE,"yaoq47ei-afsS-ui4j-o2Ug-eN81qBYXd8bz"),subQ0,sQuery(id+"FDGlM9RexINgIxM_69.wireOp",EDGE,"itTMaZda-B3PT-bgKm-7mmb-3rBEcSrfuZUN"),sQuery(id+"FDGlM9RexINgIxM_69.wireOp",EDGE,"C7O0F2G3-Vpph-GHgU-Pl9N-YHT5ADbRXPIf"),sQuery(id+"FDGlM9RexINgIxM_69.wireOp",EDGE,"orqZ82ov-6jOO-0uzi-E4WA-3w5yYGLxRUzb"),sQuery(id+"FDGlM9RexINgIxM_69.wireOp",EDGE,"c01c7ff9-4d20-4461-8e9a-ae817acbc2570.MirrorCS")])],"isStart":false})],"blendedInto":[makeQuery(id+"FvI2ILcVgUqUSgN_69.opExtrude","CAP_FACE",FACE,{"disambiguationData":[OSD([sQuery(id+"FDGlM9RexINgIxM_69.wireOp",EDGE,"U6KJ8oOa-uFEJ-GBMX-Fjwa-RUX1qTOi3xQP"),sQuery(id+"FDGlM9RexINgIxM_69.wireOp",EDGE,"074224ba-19b3-484a-b76f-18158d3281010.MirrorCS"),sQuery(id+"FDGlM9RexINgIxM_69.wireOp",EDGE,"TuuTUsh2-wWyv-E5XA-lqRk-08UfCgmNTLkA"),sQuery(id+"FDGlM9RexINgIxM_69.wireOp",EDGE,"FdSPzIjc-Apuu-YrM7-Z5xT-Lyi4e0NFlyLR"),subQ1,sQuery(id+"FDGlM9RexINgIxM_69.wireOp",EDGE,"RLFlzvnA-SoUq-z0e6-HeU4-ZmLq0tj3zLtU"),sQuery(id+"FDGlM9RexINgIxM_69.wireOp",EDGE,"2hJP9DgW-dI3q-Z07M-86yl-LCIOIgQcvf8C"),sQuery(id+"FDGlM9RexINgIxM_69.wireOp",EDGE,"yaoq47ei-afsS-ui4j-o2Ug-eN81qBYXd8bz"),subQ0,sQuery(id+"FDGlM9RexINgIxM_69.wireOp",EDGE,"itTMaZda-B3PT-bgKm-7mmb-3rBEcSrfuZUN"),sQuery(id+"FDGlM9RexINgIxM_69.wireOp",EDGE,"C7O0F2G3-Vpph-GHgU-Pl9N-YHT5ADbRXPIf"),sQuery(id+"FDGlM9RexINgIxM_69.wireOp",EDGE,"orqZ82ov-6jOO-0uzi-E4WA-3w5yYGLxRUzb"),sQuery(id+"FDGlM9RexINgIxM_69.wireOp",EDGE,"c01c7ff9-4d20-4461-8e9a-ae817acbc2570.MirrorCS")])],"isStart":false})]});}
            var Q30;
            {var subQ0=sQuery(id+"FDGlM9RexINgIxM_69.wireOp",EDGE,"7Ez0brCt-yI1f-XIkG-d1V6-Qcpqxc8gj9kZ");Q30=makeQuery(id+"FwBo9yE4fHLEFep_69.opExtrude","CAP_EDGE",EDGE,{"disambiguationData":[OSD([subQ0]),TDD([makeQuery(id+"FDGlM9RexINgIxM_69.imprint","IMPRINT",EDGE,{"disambiguationData":[TD([[makeQuery(id+"FDGlM9RexINgIxM_69.imprint","INTERSECT",VERTEX,{"derivedFrom":[subQ0,sQuery(id+"FDGlM9RexINgIxM_69.wireOp",EDGE,"RLFlzvnA-SoUq-z0e6-HeU4-ZmLq0tj3zLtU")]}),-1.0]])],"derivedFrom":subQ0})])],"isStart":true});}
            var Q31;
            Q31=makeQuery(id+"FwBo9yE4fHLEFep_69.opExtrude","CAP_EDGE",EDGE,{"disambiguationData":[OSD([sQuery(id+"FDGlM9RexINgIxM_69.wireOp",EDGE,"orqZ82ov-6jOO-0uzi-E4WA-3w5yYGLxRUzb")])],"isStart":true});
            var Q32;
            {var subQ0=sQuery(id+"FDGlM9RexINgIxM_69.wireOp",EDGE,"c01c7ff9-4d20-4461-8e9a-ae817acbc2570.MirrorCS");var subQ1=sQuery(id+"FDGlM9RexINgIxM_69.wireOp",EDGE,"orqZ82ov-6jOO-0uzi-E4WA-3w5yYGLxRUzb");var subQ2=sQuery(id+"FDGlM9RexINgIxM_69.wireOp",EDGE,"C7O0F2G3-Vpph-GHgU-Pl9N-YHT5ADbRXPIf");var subQ3=sQuery(id+"FDGlM9RexINgIxM_69.wireOp",EDGE,"itTMaZda-B3PT-bgKm-7mmb-3rBEcSrfuZUN");var subQ4=sQuery(id+"FDGlM9RexINgIxM_69.wireOp",EDGE,"qSYrSfl7-yjqs-UGFy-c140-ZDuUcCQf7A2A");var subQ5=sQuery(id+"FDGlM9RexINgIxM_69.wireOp",EDGE,"yaoq47ei-afsS-ui4j-o2Ug-eN81qBYXd8bz");var subQ6=sQuery(id+"FDGlM9RexINgIxM_69.wireOp",EDGE,"2hJP9DgW-dI3q-Z07M-86yl-LCIOIgQcvf8C");var subQ7=sQuery(id+"FDGlM9RexINgIxM_69.wireOp",EDGE,"RLFlzvnA-SoUq-z0e6-HeU4-ZmLq0tj3zLtU");var subQ8=sQuery(id+"FDGlM9RexINgIxM_69.wireOp",EDGE,"7Ez0brCt-yI1f-XIkG-d1V6-Qcpqxc8gj9kZ");var subQ9=sQuery(id+"FDGlM9RexINgIxM_69.wireOp",EDGE,"FdSPzIjc-Apuu-YrM7-Z5xT-Lyi4e0NFlyLR");var subQ10=sQuery(id+"FDGlM9RexINgIxM_69.wireOp",EDGE,"074224ba-19b3-484a-b76f-18158d3281010.MirrorCS");var subQ11=sQuery(id+"FDGlM9RexINgIxM_69.wireOp",EDGE,"U6KJ8oOa-uFEJ-GBMX-Fjwa-RUX1qTOi3xQP");Q32=makeQuery(id+"FwvY9zCnafUxNxe_69.opFillet","BLEND_EDGE",EDGE,{"blendedFrom":[makeQuery(id+"FwBo9yE4fHLEFep_69.opExtrude","SWEPT_EDGE",EDGE,{"disambiguationData":[OSD([subQ8,subQ7])]}),makeQuery(id+"FvI2ILcVgUqUSgN_69.boolean.opBoolean","MERGE",FACE,{"derivedFrom":[makeQuery(id+"FwBo9yE4fHLEFep_69.opExtrude","CAP_FACE",FACE,{"disambiguationData":[OSD([subQ11,subQ9,subQ8,subQ7,subQ6,subQ5,subQ1,sQuery(id+"FDGlM9RexINgIxM_69.wireOp",EDGE,"Me1JL4mf-vnPL-NlZd-2kHF-plJ8BSSCvuwK")])],"isStart":true}),makeQuery(id+"FwBo9yE4fHLEFep_69.opExtrude","CAP_FACE",FACE,{"disambiguationData":[OSD([subQ10,subQ9,subQ8,subQ4,subQ3,subQ2,subQ0,sQuery(id+"FDGlM9RexINgIxM_69.wireOp",EDGE,"b0834b25-e667-48a5-9b91-8a4254270c170.MirrorCS")])],"isStart":true}),makeQuery(id+"FvI2ILcVgUqUSgN_69.opExtrude","CAP_FACE",FACE,{"disambiguationData":[OSD([subQ11,subQ10,sQuery(id+"FDGlM9RexINgIxM_69.wireOp",EDGE,"TuuTUsh2-wWyv-E5XA-lqRk-08UfCgmNTLkA"),subQ9,subQ8,subQ7,subQ6,subQ5,subQ4,subQ3,subQ2,subQ1,subQ0])],"isStart":true})]})],"blendedInto":[makeQuery(id+"FvI2ILcVgUqUSgN_69.boolean.opBoolean","MERGE",FACE,{"derivedFrom":[makeQuery(id+"FwBo9yE4fHLEFep_69.opExtrude","CAP_FACE",FACE,{"disambiguationData":[OSD([subQ11,subQ9,subQ8,subQ7,subQ6,subQ5,subQ1,sQuery(id+"FDGlM9RexINgIxM_69.wireOp",EDGE,"Me1JL4mf-vnPL-NlZd-2kHF-plJ8BSSCvuwK")])],"isStart":true}),makeQuery(id+"FwBo9yE4fHLEFep_69.opExtrude","CAP_FACE",FACE,{"disambiguationData":[OSD([subQ10,subQ9,subQ8,subQ4,subQ3,subQ2,subQ0,sQuery(id+"FDGlM9RexINgIxM_69.wireOp",EDGE,"b0834b25-e667-48a5-9b91-8a4254270c170.MirrorCS")])],"isStart":true}),makeQuery(id+"FvI2ILcVgUqUSgN_69.opExtrude","CAP_FACE",FACE,{"disambiguationData":[OSD([subQ11,subQ10,sQuery(id+"FDGlM9RexINgIxM_69.wireOp",EDGE,"TuuTUsh2-wWyv-E5XA-lqRk-08UfCgmNTLkA"),subQ9,subQ8,subQ7,subQ6,subQ5,subQ4,subQ3,subQ2,subQ1,subQ0])],"isStart":true})]})]});}
            var Q33;
            Q33=makeQuery(id+"FwBo9yE4fHLEFep_69.opExtrude","CAP_EDGE",EDGE,{"disambiguationData":[OSD([sQuery(id+"FDGlM9RexINgIxM_69.wireOp",EDGE,"c01c7ff9-4d20-4461-8e9a-ae817acbc2570.MirrorCS")])],"isStart":true});
            var Q34;
            {var subQ0=sQuery(id+"FDGlM9RexINgIxM_69.wireOp",EDGE,"7Ez0brCt-yI1f-XIkG-d1V6-Qcpqxc8gj9kZ");Q34=makeQuery(id+"FwBo9yE4fHLEFep_69.opExtrude","CAP_EDGE",EDGE,{"disambiguationData":[OSD([subQ0]),TDD([makeQuery(id+"FDGlM9RexINgIxM_69.imprint","IMPRINT",EDGE,{"disambiguationData":[TD([[makeQuery(id+"FDGlM9RexINgIxM_69.imprint","INTERSECT",VERTEX,{"derivedFrom":[subQ0,sQuery(id+"FDGlM9RexINgIxM_69.wireOp",EDGE,"qSYrSfl7-yjqs-UGFy-c140-ZDuUcCQf7A2A")]}),1.0]])],"derivedFrom":subQ0})])],"isStart":true});}
            var Q35;
            {var subQ0=sQuery(id+"FDGlM9RexINgIxM_69.wireOp",EDGE,"c01c7ff9-4d20-4461-8e9a-ae817acbc2570.MirrorCS");var subQ1=sQuery(id+"FDGlM9RexINgIxM_69.wireOp",EDGE,"orqZ82ov-6jOO-0uzi-E4WA-3w5yYGLxRUzb");var subQ2=sQuery(id+"FDGlM9RexINgIxM_69.wireOp",EDGE,"C7O0F2G3-Vpph-GHgU-Pl9N-YHT5ADbRXPIf");var subQ3=sQuery(id+"FDGlM9RexINgIxM_69.wireOp",EDGE,"itTMaZda-B3PT-bgKm-7mmb-3rBEcSrfuZUN");var subQ4=sQuery(id+"FDGlM9RexINgIxM_69.wireOp",EDGE,"qSYrSfl7-yjqs-UGFy-c140-ZDuUcCQf7A2A");var subQ5=sQuery(id+"FDGlM9RexINgIxM_69.wireOp",EDGE,"yaoq47ei-afsS-ui4j-o2Ug-eN81qBYXd8bz");var subQ6=sQuery(id+"FDGlM9RexINgIxM_69.wireOp",EDGE,"2hJP9DgW-dI3q-Z07M-86yl-LCIOIgQcvf8C");var subQ7=sQuery(id+"FDGlM9RexINgIxM_69.wireOp",EDGE,"RLFlzvnA-SoUq-z0e6-HeU4-ZmLq0tj3zLtU");var subQ8=sQuery(id+"FDGlM9RexINgIxM_69.wireOp",EDGE,"7Ez0brCt-yI1f-XIkG-d1V6-Qcpqxc8gj9kZ");var subQ9=sQuery(id+"FDGlM9RexINgIxM_69.wireOp",EDGE,"FdSPzIjc-Apuu-YrM7-Z5xT-Lyi4e0NFlyLR");var subQ10=sQuery(id+"FDGlM9RexINgIxM_69.wireOp",EDGE,"074224ba-19b3-484a-b76f-18158d3281010.MirrorCS");var subQ11=sQuery(id+"FDGlM9RexINgIxM_69.wireOp",EDGE,"U6KJ8oOa-uFEJ-GBMX-Fjwa-RUX1qTOi3xQP");Q35=makeQuery(id+"FwvY9zCnafUxNxe_69.opFillet","BLEND_EDGE",EDGE,{"blendedFrom":[makeQuery(id+"FwBo9yE4fHLEFep_69.opExtrude","SWEPT_EDGE",EDGE,{"disambiguationData":[OSD([subQ8,subQ4])]}),makeQuery(id+"FvI2ILcVgUqUSgN_69.boolean.opBoolean","MERGE",FACE,{"derivedFrom":[makeQuery(id+"FwBo9yE4fHLEFep_69.opExtrude","CAP_FACE",FACE,{"disambiguationData":[OSD([subQ11,subQ9,subQ8,subQ7,subQ6,subQ5,subQ1,sQuery(id+"FDGlM9RexINgIxM_69.wireOp",EDGE,"Me1JL4mf-vnPL-NlZd-2kHF-plJ8BSSCvuwK")])],"isStart":true}),makeQuery(id+"FwBo9yE4fHLEFep_69.opExtrude","CAP_FACE",FACE,{"disambiguationData":[OSD([subQ10,subQ9,subQ8,subQ4,subQ3,subQ2,subQ0,sQuery(id+"FDGlM9RexINgIxM_69.wireOp",EDGE,"b0834b25-e667-48a5-9b91-8a4254270c170.MirrorCS")])],"isStart":true}),makeQuery(id+"FvI2ILcVgUqUSgN_69.opExtrude","CAP_FACE",FACE,{"disambiguationData":[OSD([subQ11,subQ10,sQuery(id+"FDGlM9RexINgIxM_69.wireOp",EDGE,"TuuTUsh2-wWyv-E5XA-lqRk-08UfCgmNTLkA"),subQ9,subQ8,subQ7,subQ6,subQ5,subQ4,subQ3,subQ2,subQ1,subQ0])],"isStart":true})]})],"blendedInto":[makeQuery(id+"FvI2ILcVgUqUSgN_69.boolean.opBoolean","MERGE",FACE,{"derivedFrom":[makeQuery(id+"FwBo9yE4fHLEFep_69.opExtrude","CAP_FACE",FACE,{"disambiguationData":[OSD([subQ11,subQ9,subQ8,subQ7,subQ6,subQ5,subQ1,sQuery(id+"FDGlM9RexINgIxM_69.wireOp",EDGE,"Me1JL4mf-vnPL-NlZd-2kHF-plJ8BSSCvuwK")])],"isStart":true}),makeQuery(id+"FwBo9yE4fHLEFep_69.opExtrude","CAP_FACE",FACE,{"disambiguationData":[OSD([subQ10,subQ9,subQ8,subQ4,subQ3,subQ2,subQ0,sQuery(id+"FDGlM9RexINgIxM_69.wireOp",EDGE,"b0834b25-e667-48a5-9b91-8a4254270c170.MirrorCS")])],"isStart":true}),makeQuery(id+"FvI2ILcVgUqUSgN_69.opExtrude","CAP_FACE",FACE,{"disambiguationData":[OSD([subQ11,subQ10,sQuery(id+"FDGlM9RexINgIxM_69.wireOp",EDGE,"TuuTUsh2-wWyv-E5XA-lqRk-08UfCgmNTLkA"),subQ9,subQ8,subQ7,subQ6,subQ5,subQ4,subQ3,subQ2,subQ1,subQ0])],"isStart":true})]})]});}
            var Q36;
            {var subQ0=sQuery(id+"FDGlM9RexINgIxM_69.wireOp",EDGE,"FdSPzIjc-Apuu-YrM7-Z5xT-Lyi4e0NFlyLR");Q36=makeQuery(id+"FvI2ILcVgUqUSgN_69.boolean.opBoolean","MERGE",EDGE,{"derivedFrom":[makeQuery(id+"FwBo9yE4fHLEFep_69.opExtrude","CAP_EDGE",EDGE,{"disambiguationData":[OSD([subQ0]),TDD([makeQuery(id+"FDGlM9RexINgIxM_69.imprint","IMPRINT",EDGE,{"disambiguationData":[TD([[makeQuery(id+"FDGlM9RexINgIxM_69.imprint","INTERSECT",VERTEX,{"derivedFrom":[subQ0,sQuery(id+"FDGlM9RexINgIxM_69.wireOp",EDGE,"yaoq47ei-afsS-ui4j-o2Ug-eN81qBYXd8bz")]}),-1.0]])],"derivedFrom":subQ0})])],"isStart":true}),makeQuery(id+"FwBo9yE4fHLEFep_69.opExtrude","CAP_EDGE",EDGE,{"disambiguationData":[OSD([subQ0]),TDD([makeQuery(id+"FDGlM9RexINgIxM_69.imprint","IMPRINT",EDGE,{"disambiguationData":[TD([[makeQuery(id+"FDGlM9RexINgIxM_69.imprint","INTERSECT",VERTEX,{"derivedFrom":[subQ0,sQuery(id+"FDGlM9RexINgIxM_69.wireOp",EDGE,"C7O0F2G3-Vpph-GHgU-Pl9N-YHT5ADbRXPIf")]}),1.0]])],"derivedFrom":subQ0})])],"isStart":true}),makeQuery(id+"FvI2ILcVgUqUSgN_69.opExtrude","CAP_EDGE",EDGE,{"disambiguationData":[OSD([subQ0])],"isStart":true})]});}
            var Q37;
            Q37=makeQuery(id+"FvI2ILcVgUqUSgN_69.opExtrude","CAP_EDGE",EDGE,{"disambiguationData":[OSD([sQuery(id+"FDGlM9RexINgIxM_69.wireOp",EDGE,"FdSPzIjc-Apuu-YrM7-Z5xT-Lyi4e0NFlyLR")])],"isStart":false});
            var Q38;
            Q38=makeQuery(id+"FvI2ILcVgUqUSgN_69.opExtrude","SWEPT_EDGE",EDGE,{"disambiguationData":[OSD([sQuery(id+"FDGlM9RexINgIxM_69.wireOp",EDGE,"HFHPp6yv-DVu2-IDCs-rVQe-XMDO5YvTaGjh"),sQuery(id+"FDGlM9RexINgIxM_69.wireOp",EDGE,"ml0uMYDB-3YsI-Z0xH-hTwv-6Z7Px6BG47C9")])]});
            var Q39;
            Q39=makeQuery(id+"FvI2ILcVgUqUSgN_69.opExtrude","SWEPT_EDGE",EDGE,{"disambiguationData":[OSD([sQuery(id+"FDGlM9RexINgIxM_69.wireOp",EDGE,"HFHPp6yv-DVu2-IDCs-rVQe-XMDO5YvTaGjh"),sQuery(id+"FDGlM9RexINgIxM_69.wireOp",EDGE,"iWDtfISy-sDnv-asjt-k0Gs-HZioyy7g28nr")])]});
            var Q40;
            Q40=makeQuery(id+"FvI2ILcVgUqUSgN_69.opExtrude","CAP_EDGE",EDGE,{"disambiguationData":[OSD([sQuery(id+"FDGlM9RexINgIxM_69.wireOp",EDGE,"HFHPp6yv-DVu2-IDCs-rVQe-XMDO5YvTaGjh")])],"isStart":true});
            var Q41;
            Q41=makeQuery(id+"FvI2ILcVgUqUSgN_69.opExtrude","CAP_EDGE",EDGE,{"disambiguationData":[OSD([sQuery(id+"FDGlM9RexINgIxM_69.wireOp",EDGE,"HFHPp6yv-DVu2-IDCs-rVQe-XMDO5YvTaGjh")])],"isStart":false});
            fillet(context, id + "F8", {"entities" : qUnion([Q0, Q1, Q2, Q3, Q4, Q5, Q6, Q7, Q8, Q9, Q10, Q11, Q12, Q13, Q14, Q15, Q16, Q17, Q18, Q19, Q20, Q21, Q22, Q23, Q24, Q25, Q26, Q27, Q28, Q29, Q30, Q31, Q32, Q33, Q34, Q35, Q36, Q37, Q38, Q39, Q40, Q41]), "radius" : 0.5 * mm, "tangentPropagation" : true, "allowEdgeOverflow" : false});
        }
        {
            var Q0;
            Q0=sQuery(id+"F2.wireOp",VERTEX,"E12.center");
            var Q1;
            Q1=sQuery(id+"F2.wireOp",VERTEX,"E7.end");
            var Q2;
            Q2=makeQuery(id+"F4.opExtrude","SWEPT_BODY",BODY,{"disambiguationData":[OSD([sQuery(id+"F2.wireOp",EDGE,"E3"),sQuery(id+"F2.wireOp",EDGE,"E4.MirrorC"),sQuery(id+"F2.wireOp",EDGE,"E19"),sQuery(id+"F2.wireOp",EDGE,"E20"),sQuery(id+"F2.wireOp",EDGE,"E21"),sQuery(id+"F2.wireOp",EDGE,"E22")])]});
            hole(context, id + "F9", {"style" : HoleStyle.SIMPLE, "endStyle" : HoleEndStyle.THROUGH, "holeDiameter" : 5 * mm, "isTappedThrough" : true, "tappedDepth" : 12 * mm, "tapClearance" : 3, "locations" : qUnion([Q0, Q1]), "scope" : qUnion([Q2])});
        }
    });
